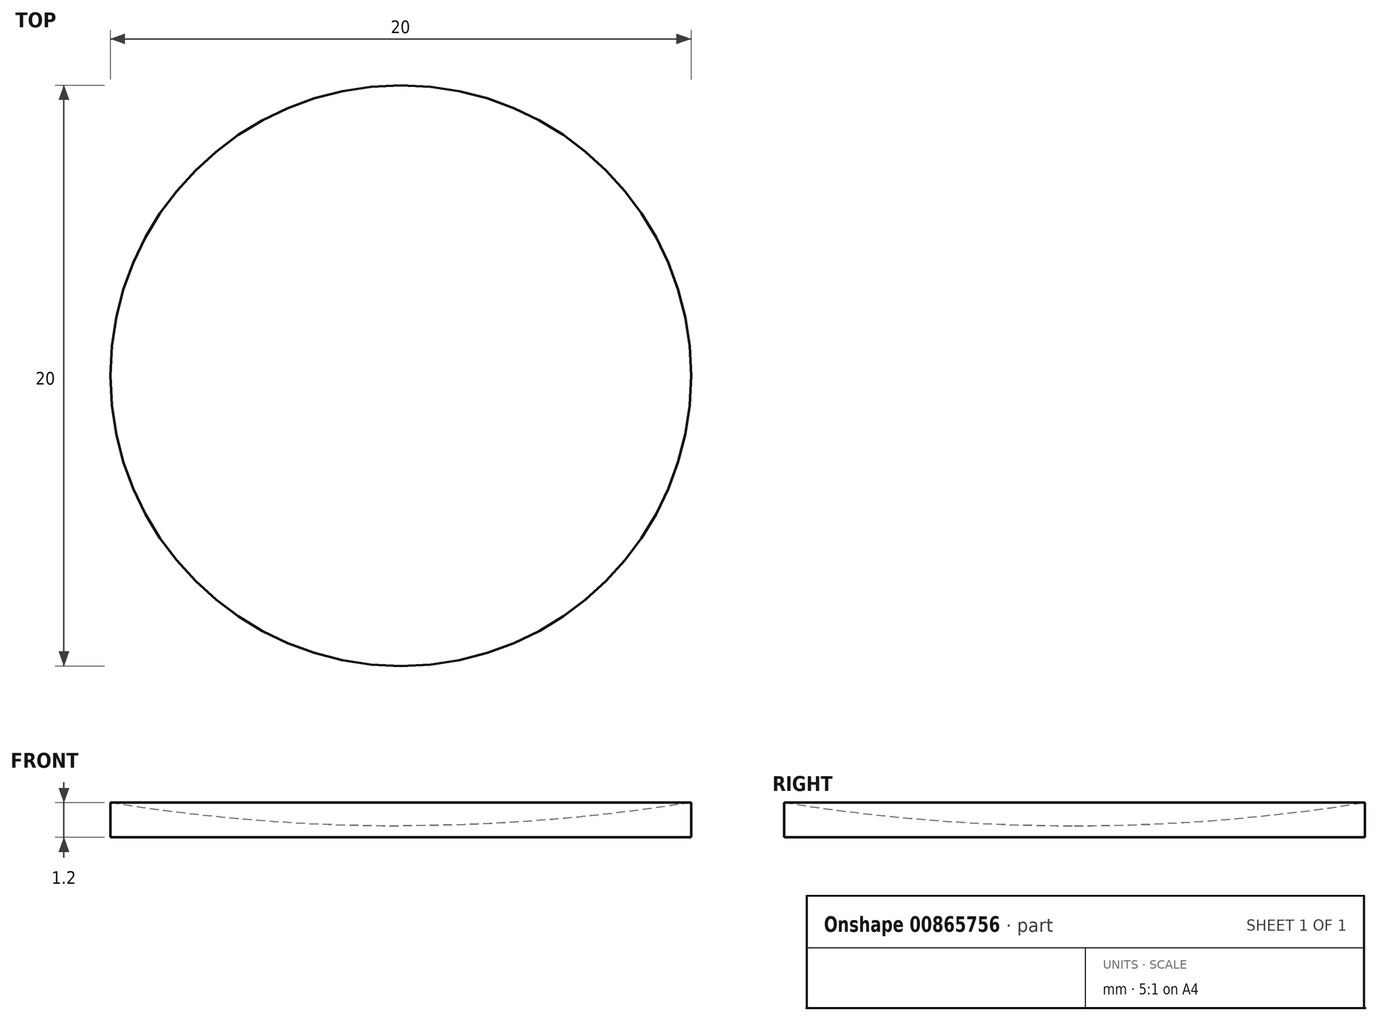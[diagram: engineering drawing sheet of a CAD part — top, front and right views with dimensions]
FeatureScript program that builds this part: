
annotation { "Feature Type Name" : "Feature", "Feature Type Description" : "" }
export const myFeature = defineFeature(function(context is Context, id is Id, definition is map)
    precondition{}
    {
        {
            var Q0;
            Q0=qCreatedBy(makeId("Top.planeOp"),FACE);
            var sketch = newSketch(context, id + "F0", { "sketchPlane" : qUnion([Q0])});
            skCircle(sketch, "E0", {"center": v(0, 0) * mm, "radius": 10 * mm});
            skSolve(sketch);
        }
        {
            var Q0;
            Q0 = qSketchRegion(id + "F0", true);
            extrude(context, id + "F1", {"entities" : qUnion([Q0]), "depth" : .2 * mm, "offsetDistance" : 25 * mm});
        }
        {
            var Q0;
            Q0=qCreatedBy(makeId("Front.planeOp"),FACE);
            var sketch = newSketch(context, id + "F2", { "sketchPlane" : qUnion([Q0])});
            skLineSegment(sketch, "E1.0", {"start": v(-10, 0.2) * mm, "end": v(10, 0.2) * mm});
            skLineSegment(sketch, "E2", {"start": v(0, 0.2) * mm, "end": v(0, 0.4) * mm});
            skLineSegment(sketch, "E3", {"start": v(10, 0.2) * mm, "end": v(10, 1.2) * mm});
            skLineSegment(sketch, "E4", {"start": v(-10, 0.2) * mm, "end": v(-10, 0.2) * mm});
            skLineSegment(sketch, "E5", {"start": v(-10, 0.2) * mm, "end": v(-10, 1.2) * mm});
            skArc(sketch, "E6", {"start": v(-10, 1.2) * mm, "mid": v(0, 0.4) * mm, "end": v(10, 1.2) * mm});
            skSolve(sketch);
        }
        {
            var Q0;
            {var subQ2=sQuery(id+"F2.wireOp",EDGE,"E2");Q0=makeQuery(id+"F2.imprint","IMPRINT",FACE,{"disambiguationData":[TD([[makeQuery(id+"F2.imprint","IMPRINT",EDGE,{"derivedFrom":subQ2}),-1.0]])]});}
            var Q1;
            Q1=sQuery(id+"F2.wireOp",EDGE,"E2");
            revolve(context, id + "F3", {"operationType" : NewBodyOperationType.ADD, "surfaceOperationType" : NewSurfaceOperationType.NEW, "entities" : qUnion([Q0]), "axis" : qUnion([Q1]), "revolveType" : RevolveType.FULL});
        }
    });
